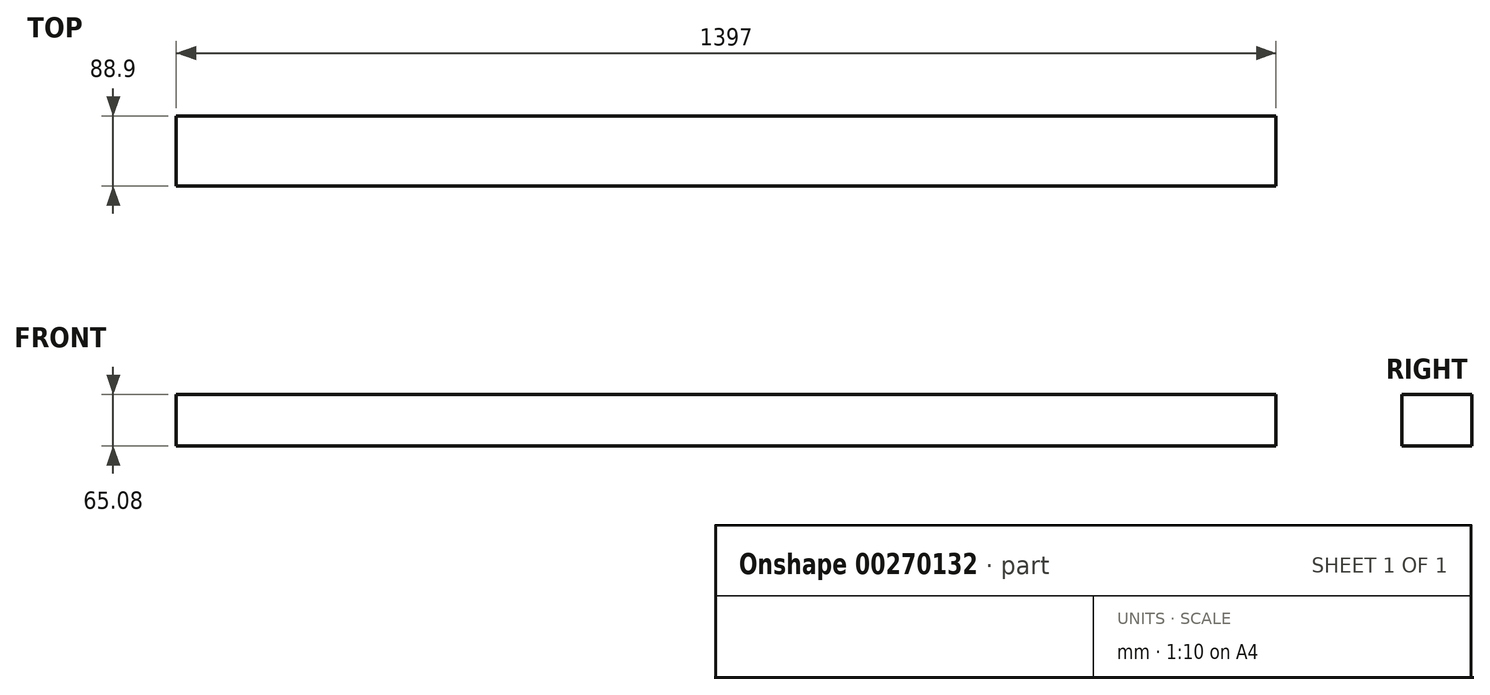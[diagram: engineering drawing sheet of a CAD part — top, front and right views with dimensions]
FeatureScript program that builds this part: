
annotation { "Feature Type Name" : "Feature", "Feature Type Description" : "" }
export const myFeature = defineFeature(function(context is Context, id is Id, definition is map)
    precondition{}
    {
        {
            var Q0;
            Q0=qCreatedBy(makeId("Front.planeOp"),FACE);
            var sketch = newSketch(context, id + "F0", { "sketchPlane" : qUnion([Q0])});
            skLineSegment(sketch, "E0.bottom", {"start": v(698.5, -32.54) * mm, "end": v(-698.5, -32.54) * mm});
            skLineSegment(sketch, "E0.top", {"start": v(698.5, 32.54) * mm, "end": v(-698.5, 32.54) * mm});
            skLineSegment(sketch, "E0.left", {"start": v(698.5, -32.54) * mm, "end": v(698.5, 32.54) * mm});
            skLineSegment(sketch, "E0.right", {"start": v(-698.5, -32.54) * mm, "end": v(-698.5, 32.54) * mm});
            skPoint(sketch, "E0.middle", {"position": v(0, 0) * mm});
            skSolve(sketch);
        }
        {
            var Q0;
            Q0=makeQuery(id+"F0.imprint","IMPRINT",FACE,{"disambiguationData":[TD([[makeQuery(id+"F0.imprint","IMPRINT",EDGE,{"derivedFrom":sQuery(id+"F0.wireOp",EDGE,"E0.bottom")}),-1.0]])]});
            extrude(context, id + "F1", {"entities" : qUnion([Q0]), "depth" : 88.9 * mm});
        }
    });
